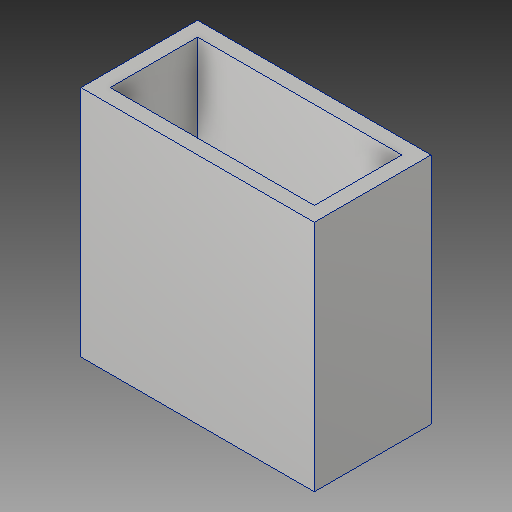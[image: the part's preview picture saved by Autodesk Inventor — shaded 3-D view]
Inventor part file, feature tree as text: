
AUTODESK INVENTOR PART (.ipt)
format: ipt  version: 2018 (Build 220112000, 112)  size: 107,008 bytes
history: native  units: in
note: dims shown in document units (in); Inventor stores cm internally (conversion verified against a paired STEP export)
features: extrude x1, sketch x1
ambient origin geometry x8: Origin, YZ Plane, XZ Plane, XY Plane, X Axis, Y Axis, Z Axis, Center Point
bodies: Solid1 (feature_tree)
feature tree (2):
  extrude  "Extrusion1"  Depth=1.0in
  sketch  "Sketch1"  dims[d0=2.0in d1=1.0in d2=0.125in d3=0.125in d4=0.125in d5=0.125in d6=2.0in d7=0.0in]
